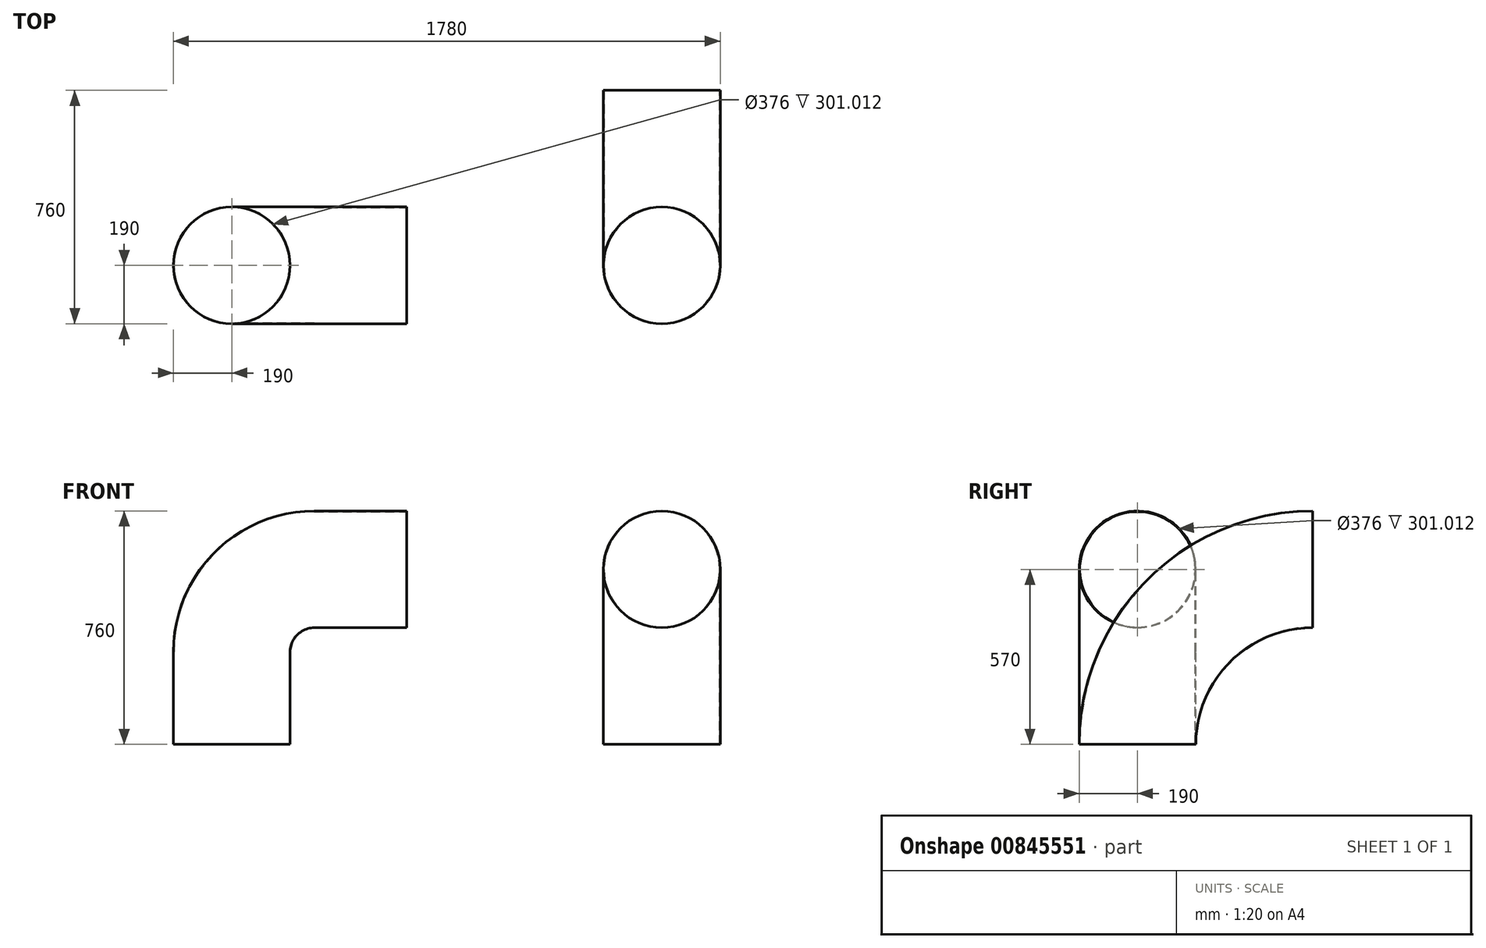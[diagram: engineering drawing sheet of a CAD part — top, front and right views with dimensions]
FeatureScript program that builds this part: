
annotation { "Feature Type Name" : "Feature", "Feature Type Description" : "" }
export const myFeature = defineFeature(function(context is Context, id is Id, definition is map)
    precondition{}
    {
        {
            var Q0;
            Q0=qCreatedBy(makeId("Top.planeOp"),FACE);
            var sketch = newSketch(context, id + "F0", { "sketchPlane" : qUnion([Q0])});
            skCircle(sketch, "E0", {"center": v(0, 0) * mm, "radius": 190 * mm});
            skCircle(sketch, "E1", {"center": v(0, 0) * mm, "radius": 188 * mm});
            skSolve(sketch);
        }
        {
            var Q0;
            Q0=qCreatedBy(makeId("Front.planeOp"),FACE);
            var sketch = newSketch(context, id + "F1", { "sketchPlane" : qUnion([Q0])});
            skLineSegment(sketch, "E2", {"start": v(0, 0) * mm, "end": v(0, 301.01) * mm});
            skLineSegment(sketch, "E3", {"start": v(268.99, 570) * mm, "end": v(570, 570) * mm});
            skArc(sketch, "E4", {"start": v(268.99, 570) * mm, "mid": v(78.78, 491.22) * mm, "end": v(0, 301.01) * mm});
            skSolve(sketch);
        }
        {
            var Q0;
            Q0=makeQuery(id+"F0.imprint","IMPRINT",FACE,{"disambiguationData":[TD([[makeQuery(id+"F0.imprint","IMPRINT",EDGE,{"derivedFrom":sQuery(id+"F0.wireOp",EDGE,"E0")}),1.0]])]});
            var Q1;
            Q1=sQuery(id+"F1.wireOp",EDGE,"E2");
            var Q2;
            Q2=sQuery(id+"F1.wireOp",EDGE,"E4");
            var Q3;
            Q3=sQuery(id+"F1.wireOp",EDGE,"E3");
            sweep(context, id + "F2", {"profiles" : qUnion([Q0]), "path" : qUnion([Q1, Q2, Q3])});
        }
        {
            var Q0;
            Q0=qCreatedBy(makeId("Top.planeOp"),FACE);
            var sketch = newSketch(context, id + "F3", { "sketchPlane" : qUnion([Q0])});
            skCircle(sketch, "E5", {"center": v(1400, 0) * mm, "radius": 190 * mm});
            skCircle(sketch, "E6", {"center": v(1400, 0) * mm, "radius": 188 * mm});
            skSolve(sketch);
        }
        {
            var Q0;
            Q0=qCreatedBy(makeId("Right.planeOp"),FACE);
            var sketch = newSketch(context, id + "F4", { "sketchPlane" : qUnion([Q0])});
            skLineSegment(sketch, "E7", {"start": v(190, 0) * mm, "end": v(190, 0) * mm});
            skLineSegment(sketch, "E8", {"start": v(570, 380) * mm, "end": v(570, 380) * mm});
            skArc(sketch, "E9", {"start": v(570, 380) * mm, "mid": v(301.3, 268.7) * mm, "end": v(190, 0) * mm});
            skSolve(sketch);
        }
        {
            var Q0;
            Q0=makeQuery(id+"F3.imprint","IMPRINT",FACE,{"disambiguationData":[TD([[makeQuery(id+"F3.imprint","IMPRINT",EDGE,{"derivedFrom":sQuery(id+"F3.wireOp",EDGE,"E5")}),1.0]])]});
            var Q1;
            Q1=sQuery(id+"F4.wireOp",EDGE,"E7");
            var Q2;
            Q2=sQuery(id+"F4.wireOp",EDGE,"E9");
            var Q3;
            Q3=sQuery(id+"F4.wireOp",EDGE,"E8");
            sweep(context, id + "F5", {"profiles" : qUnion([Q0]), "path" : qUnion([Q1, Q2, Q3])});
        }
        {
            var Q0;
            Q0=qCreatedBy(makeId("Right.planeOp"),FACE);
            cPlane(context, id + "F6", {"entities" : qUnion([Q0]), "cplaneType" : CPlaneType.OFFSET, "offset" : 1400 * mm, "width" : 150 * mm, "height" : 150 * mm});
        }
    });
